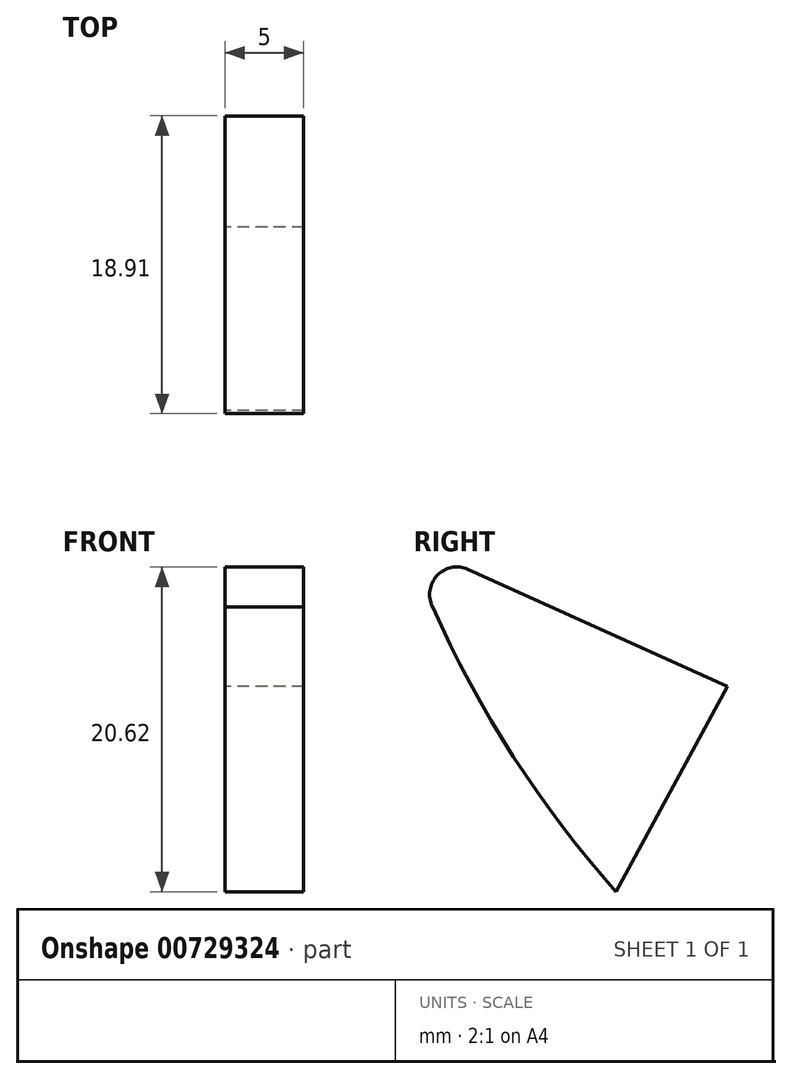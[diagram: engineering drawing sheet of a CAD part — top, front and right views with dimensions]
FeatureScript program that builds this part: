
annotation { "Feature Type Name" : "Feature", "Feature Type Description" : "" }
export const myFeature = defineFeature(function(context is Context, id is Id, definition is map)
    precondition{}
    {
        {
            var Q0;
            Q0=qCreatedBy(makeId("Right.planeOp"),FACE);
            var sketch = newSketch(context, id + "F0", { "sketchPlane" : qUnion([Q0])});
            skLineSegment(sketch, "E0", {"start": v(-9.4, 20.47) * mm, "end": v(7.06, 13.03) * mm});
            skArc(sketch, "E1", {"start": v(-11.74, 18.29) * mm, "mid": v(-6.6, 8.68) * mm, "end": v(0, 0) * mm});
            skPoint(sketch, "E2.start.orphan", {"position": v(-256.74, 59.45) * mm});
            skLineSegment(sketch, "E3", {"start": v(-9.4, 20.47) * mm, "end": v(-9.4, 20.47) * mm});
            skArc(sketch, "E4", {"start": v(-9.4, 20.47) * mm, "mid": v(-11.37, 20.09) * mm, "end": v(-11.66, 18.1) * mm});
            skLineSegment(sketch, "E5", {"start": v(0, 0) * mm, "end": v(7.06, 13.03) * mm});
            skSolve(sketch);
        }
        {
            var Q0;
            Q0=qSketchRegion(id+"F0",true);
            extrude(context, id + "F1", {"entities" : qUnion([Q0]), "depth" : 5 * mm, "offsetDistance" : 25 * mm});
        }
    });
